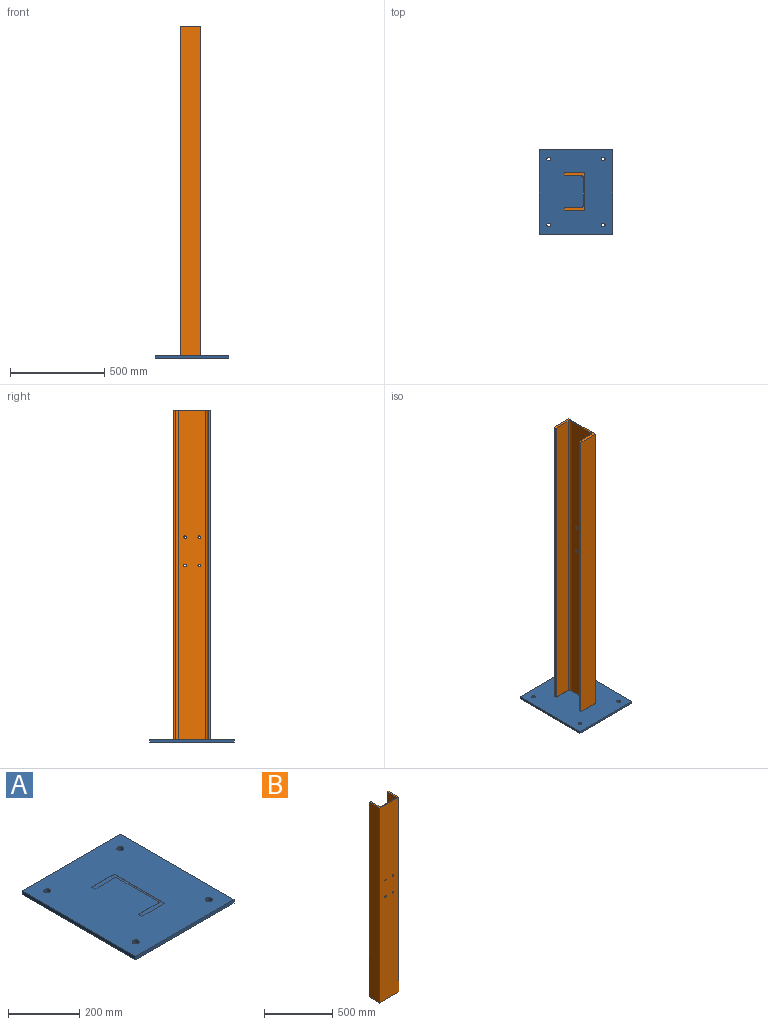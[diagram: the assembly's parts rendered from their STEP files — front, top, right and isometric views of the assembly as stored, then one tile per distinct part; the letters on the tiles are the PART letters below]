
ASSEMBLY  parts=2 mates=1
PART A: 19 faces, bbox 390x450x12 mm
  f0: plane 390x12mm, normal (0,-1,0), area 4680mm2, adj f1,f15,f16,f17
  f1: plane 450x12mm, normal (1,0,0), area 5400mm2, adj f0,f2,f16,f17
  f2: plane 390x12mm, normal (0,1,0), area 4680mm2, adj f1,f15,f16,f17
  f3: plane 90x1mm, normal (0,-1,0), area 90mm2, adj f4,f10,f16,f18
  f4: plane 200x1mm, normal (-1,0,0), area 200mm2, adj f3,f5,f16,f18
  f5: plane 90x1mm, normal (0,1,0), area 90mm2, adj f4,f6,f16,f18
  f6: plane 14x1mm, normal (1,0,0), area 14mm2, adj f5,f7,f16,f18
  f7: plane 83x1mm, normal (0,-1,0), area 83mm2, adj f6,f8,f16,f18
  f8: plane 172x1mm, normal (1,0,0), area 172mm2, adj f7,f9,f16,f18
  f9: plane 83x1mm, normal (0,1,0), area 83mm2, adj f8,f10,f16,f18
  f10: plane 14x1mm, normal (1,0,0), area 14mm2, adj f3,f9,f16,f18
  f11: cylinder r=10mm len=20mm, axis (0,0,-1), area 754mm2, adj f16,f17
  f12: cylinder r=10mm len=20mm, axis (0,0,-1), area 754mm2, adj f16,f17
  f13: cylinder r=10mm len=20mm, axis (0,0,-1), area 754mm2, adj f16,f17
  f14: cylinder r=10mm len=20mm, axis (0,0,-1), area 754mm2, adj f16,f17
  f15: plane 450x12mm, normal (-1,0,0), area 5400mm2, adj f0,f2,f16,f17
  f16: plane 450x390mm, normal (0,0,1), area 170519.4mm2, adj f0,f1,f2,f3,f4,f5,f6,f7
  f17: plane 450x390mm, normal (0,0,-1), area 174243.4mm2, adj f0,f1,f2,f11,f12,f13,f14,f15
  f18: plane 200x90mm, normal (0,0,1), area 3724mm2, adj f3,f4,f5,f6,f7,f8,f9,f10
PART B: 16 faces, bbox 200x107.9x1750 mm
  f0: plane 1750x88.89mm, normal (1,0,0), area 155562.7mm2, adj f1,f9,f10,f11
  f1: plane 1750x14mm, normal (0,1,0), area 24500mm2, adj f0,f2,f10,f11
  f2: plane 1750x107.89mm, normal (-1,0,0), area 188812.7mm2, adj f1,f3,f10,f11
  f3: plane 1750x200mm, normal (0,-1,0), area 349384.2mm2, adj f2,f4,f10,f11,f12,f13,f14,f15
  f4: plane 1750x107.89mm, normal (1,0,0), area 188812.7mm2, adj f3,f5,f10,f11
  f5: plane 1750x14mm, normal (0,1,0), area 24500mm2, adj f4,f6,f10,f11
  f6: plane 1750x88.89mm, normal (-1,0,0), area 155562.7mm2, adj f5,f7,f10,f11
  f7: cylinder r=12mm len=1750mm, axis (0,0,-1), area 32986.7mm2, adj f6,f8,f10,f11
  f8: plane 1750x148mm, normal (0,1,0), area 258384.2mm2, adj f7,f9,f10,f11,f12,f13,f14,f15
  f9: cylinder r=12mm len=1750mm, axis (0,0,-1), area 32986.7mm2, adj f0,f8,f10,f11
  f10: plane 200x107.89mm, normal (0,0,1), area 4286.8mm2, adj f0,f1,f2,f3,f4,f5,f6,f7
  f11: plane 200x107.89mm, normal (0,0,-1), area 4286.8mm2, adj f0,f1,f2,f3,f4,f5,f6,f7
  f12: cylinder r=7mm len=14mm, axis (0,-1,0), area 307.9mm2, adj f3,f8
  f13: cylinder r=7mm len=14mm, axis (0,-1,0), area 307.9mm2, adj f3,f8
  f14: cylinder r=7mm len=14mm, axis (0,-1,0), area 307.9mm2, adj f3,f8
  f15: cylinder r=7mm len=14mm, axis (0,-1,0), area 307.9mm2, adj f3,f8
PLACE A t=(85.69,512.45,-1203.17)mm
PLACE B rot(axis=(0,0,1),90deg) t=(76.74,512.45,-1191.17)mm
MATE fastened B.f11 <-> A.f16  axis (0,0,-1) through (123.69,512.45,-1191.17)mm
